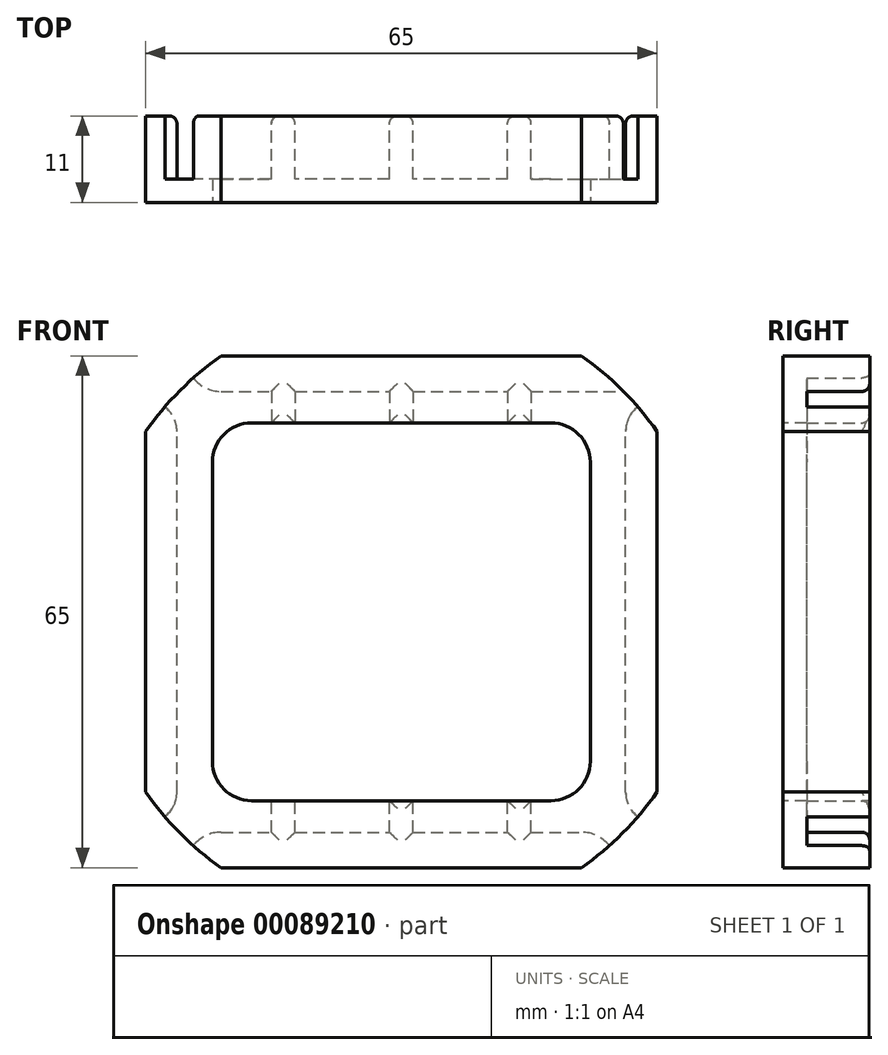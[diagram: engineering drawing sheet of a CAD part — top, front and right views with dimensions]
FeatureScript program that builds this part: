
annotation { "Feature Type Name" : "Feature", "Feature Type Description" : "" }
export const myFeature = defineFeature(function(context is Context, id is Id, definition is map)
    precondition{}
    {
        {
            var Q0;
            Q0=qCreatedBy(makeId("Front.planeOp"),FACE);
            var sketch = newSketch(context, id + "F0", { "sketchPlane" : qUnion([Q0])});
            skLineSegment(sketch, "E0.bottom", {"start": v(0, 0) * mm, "end": v(12, 0) * mm});
            skLineSegment(sketch, "E0.top", {"start": v(0, 56) * mm, "end": v(12, 56) * mm});
            skLineSegment(sketch, "E0.left", {"start": v(0, 0) * mm, "end": v(0, 56) * mm});
            skLineSegment(sketch, "E0.right", {"start": v(57, 0) * mm, "end": v(57, 56) * mm});
            skLineSegment(sketch, "E1.bottom", {"start": v(-4, 60.5) * mm, "end": v(61, 60.5) * mm});
            skLineSegment(sketch, "E1.top", {"start": v(-4, -4.5) * mm, "end": v(61, -4.5) * mm});
            skLineSegment(sketch, "E1.left", {"start": v(-4, 60.5) * mm, "end": v(-4, -4.5) * mm});
            skLineSegment(sketch, "E1.right", {"start": v(61, 60.5) * mm, "end": v(61, -4.5) * mm});
            skLineSegment(sketch, "E2.top", {"start": v(12, 52) * mm, "end": v(15, 52) * mm});
            skLineSegment(sketch, "E2.left", {"start": v(12, 56) * mm, "end": v(12, 52) * mm});
            skLineSegment(sketch, "E2.right", {"start": v(15, 56) * mm, "end": v(15, 52) * mm});
            skPoint(sketch, "E3.oppositeSnap0", {"position": v(30, 56) * mm});
            skLineSegment(sketch, "E3.top", {"start": v(27, 52) * mm, "end": v(30, 52) * mm});
            skLineSegment(sketch, "E3.left", {"start": v(27, 56) * mm, "end": v(27, 52) * mm});
            skLineSegment(sketch, "E3.right", {"start": v(30, 56) * mm, "end": v(30, 52) * mm});
            skLineSegment(sketch, "E4.top", {"start": v(42, 52) * mm, "end": v(45, 52) * mm});
            skLineSegment(sketch, "E4.left", {"start": v(42, 56) * mm, "end": v(42, 52) * mm});
            skLineSegment(sketch, "E4.right", {"start": v(45, 56) * mm, "end": v(45, 52) * mm});
            skLineSegment(sketch, "E5.top", {"start": v(12, 4) * mm, "end": v(15, 4) * mm});
            skLineSegment(sketch, "E5.left", {"start": v(12, 0) * mm, "end": v(12, 4) * mm});
            skLineSegment(sketch, "E5.right", {"start": v(15, 0) * mm, "end": v(15, 4) * mm});
            skLineSegment(sketch, "E6.top", {"start": v(27, 4) * mm, "end": v(30, 4) * mm});
            skLineSegment(sketch, "E6.left", {"start": v(27, 0) * mm, "end": v(27, 4) * mm});
            skLineSegment(sketch, "E6.right", {"start": v(30, 0) * mm, "end": v(30, 4) * mm});
            skLineSegment(sketch, "E7.top", {"start": v(42, 4) * mm, "end": v(45, 4) * mm});
            skLineSegment(sketch, "E7.left", {"start": v(42, 0) * mm, "end": v(42, 4) * mm});
            skLineSegment(sketch, "E7.right", {"start": v(45, 0) * mm, "end": v(45, 4) * mm});
            skLineSegment(sketch, "E8.trimOffspring", {"start": v(15, 56) * mm, "end": v(27, 56) * mm});
            skLineSegment(sketch, "E9.trimOffspring", {"start": v(30, 56) * mm, "end": v(42, 56) * mm});
            skLineSegment(sketch, "E10.trimOffspring", {"start": v(45, 56) * mm, "end": v(57, 56) * mm});
            skLineSegment(sketch, "E11.trimOffspring", {"start": v(30, 0) * mm, "end": v(42, 0) * mm});
            skLineSegment(sketch, "E12.trimOffspring", {"start": v(15, 0) * mm, "end": v(27, 0) * mm});
            skLineSegment(sketch, "E13.trimOffspring", {"start": v(45, 0) * mm, "end": v(57, 0) * mm});
            skSolve(sketch);
        }
        {
            var Q0;
            Q0=makeQuery(id+"F0.imprint","IMPRINT",FACE,{"disambiguationData":[TD([[makeQuery(id+"F0.imprint","IMPRINT",EDGE,{"derivedFrom":sQuery(id+"F0.wireOp",EDGE,"E0.bottom")}),-1.0]])]});
            extrude(context, id + "F1", {"entities" : qUnion([Q0]), "depth" : 8 * mm});
        }
        {
            var Q0;
            Q0=makeQuery(id+"F1.opExtrude","CAP_FACE",FACE,{"disambiguationData":[OSD([sQuery(id+"F0.wireOp",EDGE,"E0.bottom"),sQuery(id+"F0.wireOp",EDGE,"E0.top"),sQuery(id+"F0.wireOp",EDGE,"E0.left"),sQuery(id+"F0.wireOp",EDGE,"E0.right"),sQuery(id+"F0.wireOp",EDGE,"E1.bottom"),sQuery(id+"F0.wireOp",EDGE,"E1.top"),sQuery(id+"F0.wireOp",EDGE,"E1.left"),sQuery(id+"F0.wireOp",EDGE,"E1.right"),sQuery(id+"F0.wireOp",EDGE,"E2.top"),sQuery(id+"F0.wireOp",EDGE,"E2.left"),sQuery(id+"F0.wireOp",EDGE,"E2.right"),sQuery(id+"F0.wireOp",EDGE,"E3.top"),sQuery(id+"F0.wireOp",EDGE,"E3.left"),sQuery(id+"F0.wireOp",EDGE,"E3.right"),sQuery(id+"F0.wireOp",EDGE,"E4.top"),sQuery(id+"F0.wireOp",EDGE,"E4.left"),sQuery(id+"F0.wireOp",EDGE,"E4.right"),sQuery(id+"F0.wireOp",EDGE,"E5.top"),sQuery(id+"F0.wireOp",EDGE,"E5.left"),sQuery(id+"F0.wireOp",EDGE,"E5.right"),sQuery(id+"F0.wireOp",EDGE,"E6.top"),sQuery(id+"F0.wireOp",EDGE,"E6.left"),sQuery(id+"F0.wireOp",EDGE,"E6.right"),sQuery(id+"F0.wireOp",EDGE,"E7.top"),sQuery(id+"F0.wireOp",EDGE,"E7.left"),sQuery(id+"F0.wireOp",EDGE,"E7.right"),sQuery(id+"F0.wireOp",EDGE,"E8.trimOffspring"),sQuery(id+"F0.wireOp",EDGE,"E9.trimOffspring"),sQuery(id+"F0.wireOp",EDGE,"E10.trimOffspring"),sQuery(id+"F0.wireOp",EDGE,"E11.trimOffspring"),sQuery(id+"F0.wireOp",EDGE,"E12.trimOffspring"),sQuery(id+"F0.wireOp",EDGE,"E13.trimOffspring")])],"isStart":false});
            var sketch = newSketch(context, id + "F2", { "sketchPlane" : qUnion([Q0])});
            skLineSegment(sketch, "E14.bottom", {"start": v(-4, 60.5) * mm, "end": v(61, 60.5) * mm});
            skLineSegment(sketch, "E14.top", {"start": v(-4, -4.5) * mm, "end": v(61, -4.5) * mm});
            skLineSegment(sketch, "E14.left", {"start": v(-4, 60.5) * mm, "end": v(-4, -4.5) * mm});
            skLineSegment(sketch, "E14.right", {"start": v(61, 60.5) * mm, "end": v(61, -4.5) * mm});
            skSolve(sketch);
        }
        {
            var Q0;
            Q0=makeQuery(id+"F2.imprint","IMPRINT",FACE,{"disambiguationData":[TD([[makeQuery(id+"F2.imprint","IMPRINT",EDGE,{"derivedFrom":makeQuery(id+"F1.opExtrude","CAP_EDGE",EDGE,{"disambiguationData":[OSD([sQuery(id+"F0.wireOp",EDGE,"E0.bottom")])],"isStart":false})}),1.0]])]});
            var Q1;
            Q1=makeQuery(id+"F2.imprint","IMPRINT",FACE,{"disambiguationData":[TD([[makeQuery(id+"F2.imprint","IMPRINT",EDGE,{"derivedFrom":sQuery(id+"F2.wireOp",EDGE,"E14.bottom")}),-1.0]])]});
            extrude(context, id + "F3", {"entities" : qUnion([Q0, Q1]), "operationType" : NewBodyOperationType.ADD, "depth" : 3 * mm});
        }
        {
            var Q0;
            Q0=makeQuery(id+"F3.opExtrude","CAP_FACE",FACE,{"disambiguationData":[OSD([sQuery(id+"F2.wireOp",EDGE,"E14.bottom"),sQuery(id+"F2.wireOp",EDGE,"E14.top"),sQuery(id+"F2.wireOp",EDGE,"E14.left"),sQuery(id+"F2.wireOp",EDGE,"E14.right"),sQuery(id+"F2.wireOp",EDGE,"plJyJf5s-3B0M-aNOP-gcGm-lkAeHqAqfrEe.bottom"),sQuery(id+"F2.wireOp",EDGE,"plJyJf5s-3B0M-aNOP-gcGm-lkAeHqAqfrEe.top"),sQuery(id+"F2.wireOp",EDGE,"plJyJf5s-3B0M-aNOP-gcGm-lkAeHqAqfrEe.left"),sQuery(id+"F2.wireOp",EDGE,"plJyJf5s-3B0M-aNOP-gcGm-lkAeHqAqfrEe.right"),sQuery(id+"F2.wireOp",EDGE,"Hex7K4qQ-OuE8-NgdC-BP4d-HifyKzSyQ26C.bottom"),sQuery(id+"F2.wireOp",EDGE,"Hex7K4qQ-OuE8-NgdC-BP4d-HifyKzSyQ26C.top"),sQuery(id+"F2.wireOp",EDGE,"Hex7K4qQ-OuE8-NgdC-BP4d-HifyKzSyQ26C.left"),sQuery(id+"F2.wireOp",EDGE,"Hex7K4qQ-OuE8-NgdC-BP4d-HifyKzSyQ26C.right"),sQuery(id+"F2.wireOp",EDGE,"I67q2sWf-5I4z-RgrB-SqjG-KF4EHSkUAQe1.bottom"),sQuery(id+"F2.wireOp",EDGE,"I67q2sWf-5I4z-RgrB-SqjG-KF4EHSkUAQe1.top"),sQuery(id+"F2.wireOp",EDGE,"I67q2sWf-5I4z-RgrB-SqjG-KF4EHSkUAQe1.left"),sQuery(id+"F2.wireOp",EDGE,"I67q2sWf-5I4z-RgrB-SqjG-KF4EHSkUAQe1.right")])],"isStart":false});
            var sketch = newSketch(context, id + "F4", { "sketchPlane" : qUnion([Q0])});
            skLineSegment(sketch, "E15.bottom", {"start": v(47.5, 4) * mm, "end": v(9.5, 4) * mm});
            skLineSegment(sketch, "E15.top", {"start": v(47.5, 52) * mm, "end": v(9.5, 52) * mm});
            skLineSegment(sketch, "E15.left", {"start": v(52.5, 9) * mm, "end": v(52.5, 47) * mm});
            skLineSegment(sketch, "E15.right", {"start": v(4.5, 9) * mm, "end": v(4.5, 47) * mm});
            skPoint(sketch, "E15.middle", {"position": v(28.5, 28) * mm});
            skPoint(sketch, "E16.visualSharp", {"position": v(4.5, 52) * mm});
            skArc(sketch, "E16.filletArc", {"start": v(9.5, 52) * mm, "mid": v(5.96, 50.54) * mm, "end": v(4.5, 47) * mm});
            skPoint(sketch, "E17.visualSharp", {"position": v(52.5, 52) * mm});
            skArc(sketch, "E17.filletArc", {"start": v(52.5, 47) * mm, "mid": v(51.04, 50.54) * mm, "end": v(47.5, 52) * mm});
            skPoint(sketch, "E18.visualSharp", {"position": v(52.5, 4) * mm});
            skArc(sketch, "E18.filletArc", {"start": v(47.5, 4) * mm, "mid": v(51.04, 5.46) * mm, "end": v(52.5, 9) * mm});
            skPoint(sketch, "E19.visualSharp", {"position": v(4.5, 4) * mm});
            skArc(sketch, "E19.filletArc", {"start": v(4.5, 9) * mm, "mid": v(5.96, 5.46) * mm, "end": v(9.5, 4) * mm});
            skSolve(sketch);
        }
        {
            var Q0;
            Q0=makeQuery(id+"F4.imprint","IMPRINT",FACE,{"disambiguationData":[TD([[makeQuery(id+"F4.imprint","IMPRINT",EDGE,{"derivedFrom":sQuery(id+"F4.wireOp",EDGE,"E15.bottom")}),-1.0]])]});
            extrude(context, id + "F5", {"entities" : qUnion([Q0]), "operationType" : NewBodyOperationType.REMOVE, "endBound" : BoundingType.THROUGH_ALL, "oppositeDirection" : true, "depth" : 25 * mm});
        }
        {
            var Q0;
            Q0=makeQuery(id+"F3.opExtrude","CAP_FACE",FACE,{"disambiguationData":[OSD([sQuery(id+"F2.wireOp",EDGE,"E14.bottom"),sQuery(id+"F2.wireOp",EDGE,"E14.top"),sQuery(id+"F2.wireOp",EDGE,"E14.left"),sQuery(id+"F2.wireOp",EDGE,"E14.right"),sQuery(id+"F2.wireOp",EDGE,"plJyJf5s-3B0M-aNOP-gcGm-lkAeHqAqfrEe.bottom"),sQuery(id+"F2.wireOp",EDGE,"plJyJf5s-3B0M-aNOP-gcGm-lkAeHqAqfrEe.top"),sQuery(id+"F2.wireOp",EDGE,"plJyJf5s-3B0M-aNOP-gcGm-lkAeHqAqfrEe.left"),sQuery(id+"F2.wireOp",EDGE,"plJyJf5s-3B0M-aNOP-gcGm-lkAeHqAqfrEe.right"),sQuery(id+"F2.wireOp",EDGE,"Hex7K4qQ-OuE8-NgdC-BP4d-HifyKzSyQ26C.bottom"),sQuery(id+"F2.wireOp",EDGE,"Hex7K4qQ-OuE8-NgdC-BP4d-HifyKzSyQ26C.top"),sQuery(id+"F2.wireOp",EDGE,"Hex7K4qQ-OuE8-NgdC-BP4d-HifyKzSyQ26C.left"),sQuery(id+"F2.wireOp",EDGE,"Hex7K4qQ-OuE8-NgdC-BP4d-HifyKzSyQ26C.right"),sQuery(id+"F2.wireOp",EDGE,"I67q2sWf-5I4z-RgrB-SqjG-KF4EHSkUAQe1.bottom"),sQuery(id+"F2.wireOp",EDGE,"I67q2sWf-5I4z-RgrB-SqjG-KF4EHSkUAQe1.top"),sQuery(id+"F2.wireOp",EDGE,"I67q2sWf-5I4z-RgrB-SqjG-KF4EHSkUAQe1.left"),sQuery(id+"F2.wireOp",EDGE,"I67q2sWf-5I4z-RgrB-SqjG-KF4EHSkUAQe1.right")])],"isStart":false});
            var sketch = newSketch(context, id + "F6", { "sketchPlane" : qUnion([Q0])});
            skArc(sketch, "E20", {"start": v(5.61, 60.5) * mm, "mid": v(0.4, 56.1) * mm, "end": v(-4, 50.89) * mm});
            skLineSegment(sketch, "E21", {"start": v(-4, 50.89) * mm, "end": v(-4, 5.11) * mm});
            skLineSegment(sketch, "E22", {"start": v(5.61, 60.5) * mm, "end": v(51.39, 60.5) * mm});
            skLineSegment(sketch, "E23", {"start": v(61, 50.89) * mm, "end": v(61, 5.11) * mm});
            skLineSegment(sketch, "E24", {"start": v(5.61, -4.5) * mm, "end": v(51.39, -4.5) * mm});
            skArc(sketch, "E25.trimOffspring", {"start": v(-4, 5.11) * mm, "mid": v(0.4, -0.1) * mm, "end": v(5.61, -4.5) * mm});
            skArc(sketch, "E26.trimOffspring", {"start": v(51.39, -4.5) * mm, "mid": v(56.6, -0.1) * mm, "end": v(61, 5.11) * mm});
            skArc(sketch, "E27.trimOffspring", {"start": v(61, 50.89) * mm, "mid": v(56.6, 56.1) * mm, "end": v(51.39, 60.5) * mm});
            skSolve(sketch);
        }
        {
            var Q0;
            {var subQ0=sQuery(id+"F6.wireOp",EDGE,"E20");Q0=makeQuery(id+"F6.imprint","IMPRINT",FACE,{"disambiguationData":[TD([[makeQuery(id+"F6.imprint","IMPRINT",EDGE,{"derivedFrom":subQ0}),-1.0]])]});}
            var Q1;
            {var subQ0=sQuery(id+"F6.wireOp",EDGE,"E27.trimOffspring");Q1=makeQuery(id+"F6.imprint","IMPRINT",FACE,{"disambiguationData":[TD([[makeQuery(id+"F6.imprint","IMPRINT",EDGE,{"derivedFrom":subQ0}),-1.0]])]});}
            var Q2;
            {var subQ0=sQuery(id+"F6.wireOp",EDGE,"E26.trimOffspring");Q2=makeQuery(id+"F6.imprint","IMPRINT",FACE,{"disambiguationData":[TD([[makeQuery(id+"F6.imprint","IMPRINT",EDGE,{"derivedFrom":subQ0}),-1.0]])]});}
            var Q3;
            {var subQ0=sQuery(id+"F6.wireOp",EDGE,"E25.trimOffspring");Q3=makeQuery(id+"F6.imprint","IMPRINT",FACE,{"disambiguationData":[TD([[makeQuery(id+"F6.imprint","IMPRINT",EDGE,{"derivedFrom":subQ0}),-1.0]])]});}
            extrude(context, id + "F7", {"entities" : qUnion([Q0, Q1, Q2, Q3]), "operationType" : NewBodyOperationType.REMOVE, "endBound" : BoundingType.THROUGH_ALL, "oppositeDirection" : true, "depth" : 25 * mm});
        }
        {
            var Q0;
            {var subQ0=sQuery(id+"F0.wireOp",EDGE,"E4.left");var subQ1=sQuery(id+"F0.wireOp",EDGE,"E2.top");var subQ2=sQuery(id+"F0.wireOp",EDGE,"E8.trimOffspring");var subQ3=sQuery(id+"F0.wireOp",EDGE,"E4.top");var subQ4=sQuery(id+"F0.wireOp",EDGE,"E3.right");var subQ5=sQuery(id+"F0.wireOp",EDGE,"E3.left");var subQ6=sQuery(id+"F0.wireOp",EDGE,"E3.top");var subQ7=sQuery(id+"F0.wireOp",EDGE,"E2.right");var subQ8=sQuery(id+"F0.wireOp",EDGE,"E1.bottom");var subQ9=sQuery(id+"F0.wireOp",EDGE,"E0.top");var subQ10=sQuery(id+"F0.wireOp",EDGE,"E2.left");var subQ11=sQuery(id+"F0.wireOp",EDGE,"E4.right");var subQ12=sQuery(id+"F0.wireOp",EDGE,"E9.trimOffspring");var subQ13=sQuery(id+"F0.wireOp",EDGE,"E10.trimOffspring");Q0=makeQuery(id+"F7.boolean.opBoolean","SPLIT",FACE,{"disambiguationData":[TD([makeQuery(id+"F1.opExtrude","SWEPT_FACE",FACE,{"disambiguationData":[OSD([subQ9])]})])],"derivedFrom":makeQuery(id+"F1.opExtrude","CAP_FACE",FACE,{"disambiguationData":[OSD([sQuery(id+"F0.wireOp",EDGE,"E0.bottom"),subQ9,sQuery(id+"F0.wireOp",EDGE,"E0.left"),sQuery(id+"F0.wireOp",EDGE,"E0.right"),subQ8,sQuery(id+"F0.wireOp",EDGE,"E1.top"),sQuery(id+"F0.wireOp",EDGE,"E1.left"),sQuery(id+"F0.wireOp",EDGE,"E1.right"),subQ1,subQ10,subQ7,subQ6,subQ5,subQ4,subQ3,subQ0,subQ11,sQuery(id+"F0.wireOp",EDGE,"E5.top"),sQuery(id+"F0.wireOp",EDGE,"E5.left"),sQuery(id+"F0.wireOp",EDGE,"E5.right"),sQuery(id+"F0.wireOp",EDGE,"E6.top"),sQuery(id+"F0.wireOp",EDGE,"E6.left"),sQuery(id+"F0.wireOp",EDGE,"E6.right"),sQuery(id+"F0.wireOp",EDGE,"E7.top"),sQuery(id+"F0.wireOp",EDGE,"E7.left"),sQuery(id+"F0.wireOp",EDGE,"E7.right"),subQ2,subQ12,subQ13,sQuery(id+"F0.wireOp",EDGE,"E11.trimOffspring"),sQuery(id+"F0.wireOp",EDGE,"E12.trimOffspring"),sQuery(id+"F0.wireOp",EDGE,"E13.trimOffspring")])],"isStart":true})});}
            var sketch = newSketch(context, id + "F8", { "sketchPlane" : qUnion([Q0])});
            skLineSegment(sketch, "E28", {"start": v(-73.5, 28) * mm, "end": v(33.98, 28) * mm, "construction": true});
            skLineSegment(sketch, "E29.bottom", {"start": v(-55.89, 60.5) * mm, "end": v(-61, 60.5) * mm});
            skLineSegment(sketch, "E29.top", {"start": v(-51.39, 50.89) * mm, "end": v(-57, 50.89) * mm});
            skLineSegment(sketch, "E29.left", {"start": v(-51.39, 56) * mm, "end": v(-51.39, 50.89) * mm});
            skArc(sketch, "E30", {"start": v(-57, 50.89) * mm, "mid": v(-58.74, 54.2) * mm, "end": v(-62.46, 54.61) * mm});
            skArc(sketch, "E31", {"start": v(-51.39, 56) * mm, "mid": v(-54.57, 57.32) * mm, "end": v(-55.89, 60.5) * mm});
            skLineSegment(sketch, "E32", {"start": v(-62.46, 54.61) * mm, "end": v(-61, 60.5) * mm});
            skPoint(sketch, "E33.center", {"position": v(-28.5, 28) * mm});
            skLineSegment(sketch, "E34", {"start": v(-28.5, 72.63) * mm, "end": v(-28.5, -22.48) * mm, "construction": true});
            skLineSegment(sketch, "E35.MirrorCS", {"start": v(5.46, 54.61) * mm, "end": v(4, 60.5) * mm});
            skLineSegment(sketch, "E36.MirrorCS", {"start": v(-1.11, 60.5) * mm, "end": v(4, 60.5) * mm});
            skArc(sketch, "E37.MirrorCS", {"start": v(-5.61, 56) * mm, "mid": v(-2.43, 57.32) * mm, "end": v(-1.11, 60.5) * mm});
            skLineSegment(sketch, "E38.MirrorCS", {"start": v(-5.61, 56) * mm, "end": v(-5.61, 50.89) * mm});
            skLineSegment(sketch, "E39.MirrorCS", {"start": v(-5.61, 50.89) * mm, "end": v(0, 50.89) * mm});
            skArc(sketch, "E40.MirrorCS", {"start": v(0, 50.89) * mm, "mid": v(1.74, 54.2) * mm, "end": v(5.46, 54.61) * mm});
            skLineSegment(sketch, "E41.MirrorCS", {"start": v(-62.46, 1.39) * mm, "end": v(-61, -4.5) * mm});
            skLineSegment(sketch, "E42.MirrorCS", {"start": v(-55.89, -4.5) * mm, "end": v(-61, -4.5) * mm});
            skArc(sketch, "E43.MirrorCS", {"start": v(-51.39, 0) * mm, "mid": v(-54.57, -1.32) * mm, "end": v(-55.89, -4.5) * mm});
            skArc(sketch, "E44.MirrorCS", {"start": v(-57, 5.11) * mm, "mid": v(-58.74, 1.8) * mm, "end": v(-62.46, 1.39) * mm});
            skLineSegment(sketch, "E45.MirrorCS", {"start": v(-51.39, 5.11) * mm, "end": v(-57, 5.11) * mm});
            skLineSegment(sketch, "E46.MirrorCS", {"start": v(-51.39, 0) * mm, "end": v(-51.39, 5.11) * mm});
            skLineSegment(sketch, "E47.MirrorCS", {"start": v(-5.61, 0) * mm, "end": v(-5.61, 5.11) * mm});
            skLineSegment(sketch, "E48.MirrorCS", {"start": v(-5.61, 5.11) * mm, "end": v(0, 5.11) * mm});
            skArc(sketch, "E49.MirrorCS", {"start": v(0, 5.11) * mm, "mid": v(1.74, 1.8) * mm, "end": v(5.46, 1.39) * mm});
            skLineSegment(sketch, "E50.MirrorCS", {"start": v(5.46, 1.39) * mm, "end": v(4, -4.5) * mm});
            skArc(sketch, "E51.MirrorCS", {"start": v(-5.61, 0) * mm, "mid": v(-2.43, -1.32) * mm, "end": v(-1.11, -4.5) * mm});
            skLineSegment(sketch, "E52.MirrorCS", {"start": v(-1.11, -4.5) * mm, "end": v(4, -4.5) * mm});
            skSolve(sketch);
        }
        {
            var Q0;
            {var subQ1=sQuery(id+"F8.wireOp",EDGE,"E29.bottom");Q0=makeQuery(id+"F8.imprint","IMPRINT",FACE,{"disambiguationData":[TD([[makeQuery(id+"F8.imprint","IMPRINT",EDGE,{"derivedFrom":subQ1}),1.0]])]});}
            var Q1;
            {var subQ0=sQuery(id+"F8.wireOp",EDGE,"E31");var subQ1=sQuery(id+"F0.wireOp",EDGE,"E10.trimOffspring");var subQ2=makeQuery(id+"F1.opExtrude","CAP_EDGE",EDGE,{"disambiguationData":[OSD([subQ1])],"isStart":true});var subQ3=makeQuery(id+"F8.imprint","INTERSECT",VERTEX,{"derivedFrom":[subQ2,sQuery(id+"F8.wireOp",EDGE,"E29.left"),subQ0]});Q1=makeQuery(id+"F8.imprint","IMPRINT",FACE,{"disambiguationData":[TD([[makeQuery(id+"F8.imprint","IMPRINT",EDGE,{"disambiguationData":[TD([[subQ3,-1.0]])],"derivedFrom":subQ0}),1.0]])]});}
            var Q2;
            {var subQ0=sQuery(id+"F8.wireOp",EDGE,"E37.MirrorCS");var subQ1=sQuery(id+"F0.wireOp",EDGE,"E0.top");var subQ2=makeQuery(id+"F1.opExtrude","CAP_EDGE",EDGE,{"disambiguationData":[OSD([subQ1])],"isStart":true});var subQ3=makeQuery(id+"F8.imprint","INTERSECT",VERTEX,{"derivedFrom":[subQ2,subQ0,sQuery(id+"F8.wireOp",EDGE,"E38.MirrorCS")]});Q2=makeQuery(id+"F8.imprint","IMPRINT",FACE,{"disambiguationData":[TD([[makeQuery(id+"F8.imprint","IMPRINT",EDGE,{"disambiguationData":[TD([[subQ3,-1.0]])],"derivedFrom":subQ0}),-1.0]])]});}
            var Q3;
            Q3=makeQuery(id+"F8.imprint","IMPRINT",FACE,{"disambiguationData":[TD([[makeQuery(id+"F8.imprint","IMPRINT",EDGE,{"derivedFrom":sQuery(id+"F8.wireOp",EDGE,"E35.MirrorCS")}),1.0]])]});
            var Q4;
            Q4=makeQuery(id+"F8.imprint","IMPRINT",FACE,{"disambiguationData":[TD([[makeQuery(id+"F8.imprint","IMPRINT",EDGE,{"derivedFrom":sQuery(id+"F8.wireOp",EDGE,"E47.MirrorCS")}),-1.0]])]});
            var Q5;
            Q5=makeQuery(id+"F8.imprint","IMPRINT",FACE,{"disambiguationData":[TD([[makeQuery(id+"F8.imprint","IMPRINT",EDGE,{"derivedFrom":sQuery(id+"F8.wireOp",EDGE,"E41.MirrorCS")}),1.0]])]});
            var Q6;
            {var subQ0=sQuery(id+"F2.wireOp",EDGE,"I67q2sWf-5I4z-RgrB-SqjG-KF4EHSkUAQe1.bottom");var subQ1=sQuery(id+"F2.wireOp",EDGE,"I67q2sWf-5I4z-RgrB-SqjG-KF4EHSkUAQe1.top");var subQ2=sQuery(id+"F2.wireOp",EDGE,"I67q2sWf-5I4z-RgrB-SqjG-KF4EHSkUAQe1.right");Q6=makeQuery(id+"F3.boolean.opBoolean","SPLIT",FACE,{"disambiguationData":[TD([makeQuery(id+"F1.opExtrude","SWEPT_FACE",FACE,{"disambiguationData":[OSD([sQuery(id+"F0.wireOp",EDGE,"E0.right")])]})])],"derivedFrom":makeQuery(id+"F3.opExtrude","CAP_FACE",FACE,{"disambiguationData":[OSD([sQuery(id+"F2.wireOp",EDGE,"E14.bottom"),sQuery(id+"F2.wireOp",EDGE,"E14.top"),sQuery(id+"F2.wireOp",EDGE,"E14.left"),sQuery(id+"F2.wireOp",EDGE,"E14.right"),sQuery(id+"F2.wireOp",EDGE,"plJyJf5s-3B0M-aNOP-gcGm-lkAeHqAqfrEe.bottom"),sQuery(id+"F2.wireOp",EDGE,"plJyJf5s-3B0M-aNOP-gcGm-lkAeHqAqfrEe.top"),sQuery(id+"F2.wireOp",EDGE,"plJyJf5s-3B0M-aNOP-gcGm-lkAeHqAqfrEe.left"),sQuery(id+"F2.wireOp",EDGE,"plJyJf5s-3B0M-aNOP-gcGm-lkAeHqAqfrEe.right"),sQuery(id+"F2.wireOp",EDGE,"Hex7K4qQ-OuE8-NgdC-BP4d-HifyKzSyQ26C.bottom"),sQuery(id+"F2.wireOp",EDGE,"Hex7K4qQ-OuE8-NgdC-BP4d-HifyKzSyQ26C.top"),sQuery(id+"F2.wireOp",EDGE,"Hex7K4qQ-OuE8-NgdC-BP4d-HifyKzSyQ26C.left"),sQuery(id+"F2.wireOp",EDGE,"Hex7K4qQ-OuE8-NgdC-BP4d-HifyKzSyQ26C.right"),subQ0,subQ1,sQuery(id+"F2.wireOp",EDGE,"I67q2sWf-5I4z-RgrB-SqjG-KF4EHSkUAQe1.left"),subQ2])],"isStart":true})});}
            extrude(context, id + "F9", {"entities" : qUnion([Q0, Q1, Q2, Q3, Q4, Q5]), "operationType" : NewBodyOperationType.REMOVE, "oppositeDirection" : true, "endBoundEntityFace" : qUnion([Q6]), "depth" : 8 * mm});
        }
        {
            var Q0;
            Q0=makeQuery(id+"F1.opExtrude","CAP_EDGE",EDGE,{"disambiguationData":[OSD([sQuery(id+"F0.wireOp",EDGE,"E10.trimOffspring")])],"isStart":true});
            var Q1;
            Q1=makeQuery(id+"F1.opExtrude","CAP_EDGE",EDGE,{"disambiguationData":[OSD([sQuery(id+"F0.wireOp",EDGE,"E4.right")])],"isStart":true});
            var Q2;
            Q2=makeQuery(id+"F9.boolean.opBoolean","COPY",EDGE,{"derivedFrom":makeQuery(id+"F9.opExtrude","CAP_EDGE",EDGE,{"disambiguationData":[OSD([sQuery(id+"F8.wireOp",EDGE,"E31")])],"isStart":true})});
            var Q3;
            Q3=makeQuery(id+"F1.opExtrude","CAP_EDGE",EDGE,{"disambiguationData":[OSD([sQuery(id+"F0.wireOp",EDGE,"E4.top")])],"isStart":true});
            var Q4;
            Q4=makeQuery(id+"F1.opExtrude","CAP_EDGE",EDGE,{"disambiguationData":[OSD([sQuery(id+"F0.wireOp",EDGE,"E4.left")])],"isStart":true});
            var Q5;
            Q5=makeQuery(id+"F1.opExtrude","CAP_EDGE",EDGE,{"disambiguationData":[OSD([sQuery(id+"F0.wireOp",EDGE,"E9.trimOffspring")])],"isStart":true});
            var Q6;
            Q6=makeQuery(id+"F1.opExtrude","CAP_EDGE",EDGE,{"disambiguationData":[OSD([sQuery(id+"F0.wireOp",EDGE,"E3.right")])],"isStart":true});
            var Q7;
            Q7=makeQuery(id+"F1.opExtrude","CAP_EDGE",EDGE,{"disambiguationData":[OSD([sQuery(id+"F0.wireOp",EDGE,"E3.top")])],"isStart":true});
            var Q8;
            Q8=makeQuery(id+"F1.opExtrude","CAP_EDGE",EDGE,{"disambiguationData":[OSD([sQuery(id+"F0.wireOp",EDGE,"E3.left")])],"isStart":true});
            var Q9;
            Q9=makeQuery(id+"F1.opExtrude","CAP_EDGE",EDGE,{"disambiguationData":[OSD([sQuery(id+"F0.wireOp",EDGE,"E8.trimOffspring")])],"isStart":true});
            var Q10;
            Q10=makeQuery(id+"F1.opExtrude","CAP_EDGE",EDGE,{"disambiguationData":[OSD([sQuery(id+"F0.wireOp",EDGE,"E2.right")])],"isStart":true});
            var Q11;
            Q11=makeQuery(id+"F1.opExtrude","CAP_EDGE",EDGE,{"disambiguationData":[OSD([sQuery(id+"F0.wireOp",EDGE,"E2.top")])],"isStart":true});
            var Q12;
            Q12=makeQuery(id+"F1.opExtrude","CAP_EDGE",EDGE,{"disambiguationData":[OSD([sQuery(id+"F0.wireOp",EDGE,"E2.left")])],"isStart":true});
            var Q13;
            Q13=makeQuery(id+"F1.opExtrude","CAP_EDGE",EDGE,{"disambiguationData":[OSD([sQuery(id+"F0.wireOp",EDGE,"E0.top")])],"isStart":true});
            var Q14;
            Q14=makeQuery(id+"F1.opExtrude","CAP_EDGE",EDGE,{"disambiguationData":[OSD([sQuery(id+"F0.wireOp",EDGE,"E0.right")])],"isStart":true});
            var Q15;
            Q15=makeQuery(id+"F9.boolean.opBoolean","COPY",EDGE,{"derivedFrom":makeQuery(id+"F9.opExtrude","CAP_EDGE",EDGE,{"disambiguationData":[OSD([sQuery(id+"F8.wireOp",EDGE,"E30")])],"isStart":true})});
            var Q16;
            Q16=makeQuery(id+"F9.boolean.opBoolean","COPY",EDGE,{"derivedFrom":makeQuery(id+"F9.opExtrude","CAP_EDGE",EDGE,{"disambiguationData":[OSD([sQuery(id+"F8.wireOp",EDGE,"E44.MirrorCS")])],"isStart":true})});
            var Q17;
            Q17=makeQuery(id+"F9.boolean.opBoolean","COPY",EDGE,{"derivedFrom":makeQuery(id+"F9.opExtrude","CAP_EDGE",EDGE,{"disambiguationData":[OSD([sQuery(id+"F8.wireOp",EDGE,"E43.MirrorCS")])],"isStart":true})});
            var Q18;
            Q18=makeQuery(id+"F1.opExtrude","CAP_EDGE",EDGE,{"disambiguationData":[OSD([sQuery(id+"F0.wireOp",EDGE,"E13.trimOffspring")])],"isStart":true});
            var Q19;
            Q19=makeQuery(id+"F1.opExtrude","CAP_EDGE",EDGE,{"disambiguationData":[OSD([sQuery(id+"F0.wireOp",EDGE,"E7.right")])],"isStart":true});
            var Q20;
            Q20=makeQuery(id+"F1.opExtrude","CAP_EDGE",EDGE,{"disambiguationData":[OSD([sQuery(id+"F0.wireOp",EDGE,"E7.top")])],"isStart":true});
            var Q21;
            Q21=makeQuery(id+"F1.opExtrude","CAP_EDGE",EDGE,{"disambiguationData":[OSD([sQuery(id+"F0.wireOp",EDGE,"E7.left")])],"isStart":true});
            var Q22;
            Q22=makeQuery(id+"F1.opExtrude","CAP_EDGE",EDGE,{"disambiguationData":[OSD([sQuery(id+"F0.wireOp",EDGE,"E11.trimOffspring")])],"isStart":true});
            var Q23;
            Q23=makeQuery(id+"F1.opExtrude","CAP_EDGE",EDGE,{"disambiguationData":[OSD([sQuery(id+"F0.wireOp",EDGE,"E6.right")])],"isStart":true});
            var Q24;
            Q24=makeQuery(id+"F1.opExtrude","CAP_EDGE",EDGE,{"disambiguationData":[OSD([sQuery(id+"F0.wireOp",EDGE,"E6.top")])],"isStart":true});
            var Q25;
            Q25=makeQuery(id+"F1.opExtrude","CAP_EDGE",EDGE,{"disambiguationData":[OSD([sQuery(id+"F0.wireOp",EDGE,"E6.left")])],"isStart":true});
            var Q26;
            Q26=makeQuery(id+"F1.opExtrude","CAP_EDGE",EDGE,{"disambiguationData":[OSD([sQuery(id+"F0.wireOp",EDGE,"E12.trimOffspring")])],"isStart":true});
            var Q27;
            Q27=makeQuery(id+"F1.opExtrude","CAP_EDGE",EDGE,{"disambiguationData":[OSD([sQuery(id+"F0.wireOp",EDGE,"E5.right")])],"isStart":true});
            var Q28;
            Q28=makeQuery(id+"F1.opExtrude","CAP_EDGE",EDGE,{"disambiguationData":[OSD([sQuery(id+"F0.wireOp",EDGE,"E5.left")])],"isStart":true});
            var Q29;
            Q29=makeQuery(id+"F1.opExtrude","CAP_EDGE",EDGE,{"disambiguationData":[OSD([sQuery(id+"F0.wireOp",EDGE,"E0.bottom")])],"isStart":true});
            var Q30;
            Q30=makeQuery(id+"F1.opExtrude","CAP_EDGE",EDGE,{"disambiguationData":[OSD([sQuery(id+"F0.wireOp",EDGE,"E0.left")])],"isStart":true});
            var Q31;
            Q31=makeQuery(id+"F9.boolean.opBoolean","COPY",EDGE,{"derivedFrom":makeQuery(id+"F9.opExtrude","CAP_EDGE",EDGE,{"disambiguationData":[OSD([sQuery(id+"F8.wireOp",EDGE,"E49.MirrorCS")])],"isStart":true})});
            var Q32;
            Q32=makeQuery(id+"F9.boolean.opBoolean","COPY",EDGE,{"derivedFrom":makeQuery(id+"F9.opExtrude","CAP_EDGE",EDGE,{"disambiguationData":[OSD([sQuery(id+"F8.wireOp",EDGE,"E40.MirrorCS")])],"isStart":true})});
            var Q33;
            Q33=makeQuery(id+"F9.boolean.opBoolean","COPY",EDGE,{"derivedFrom":makeQuery(id+"F9.opExtrude","CAP_EDGE",EDGE,{"disambiguationData":[OSD([sQuery(id+"F8.wireOp",EDGE,"E37.MirrorCS")])],"isStart":true})});
            fillet(context, id + "F10", {"entities" : qUnion([Q0, Q1, Q2, Q3, Q4, Q5, Q6, Q7, Q8, Q9, Q10, Q11, Q12, Q13, Q14, Q15, Q16, Q17, Q18, Q19, Q20, Q21, Q22, Q23, Q24, Q25, Q26, Q27, Q28, Q29, Q30, Q31, Q32, Q33]), "radius" : 1 * mm, "tangentPropagation" : true, "allowEdgeOverflow" : false});
        }
    });
